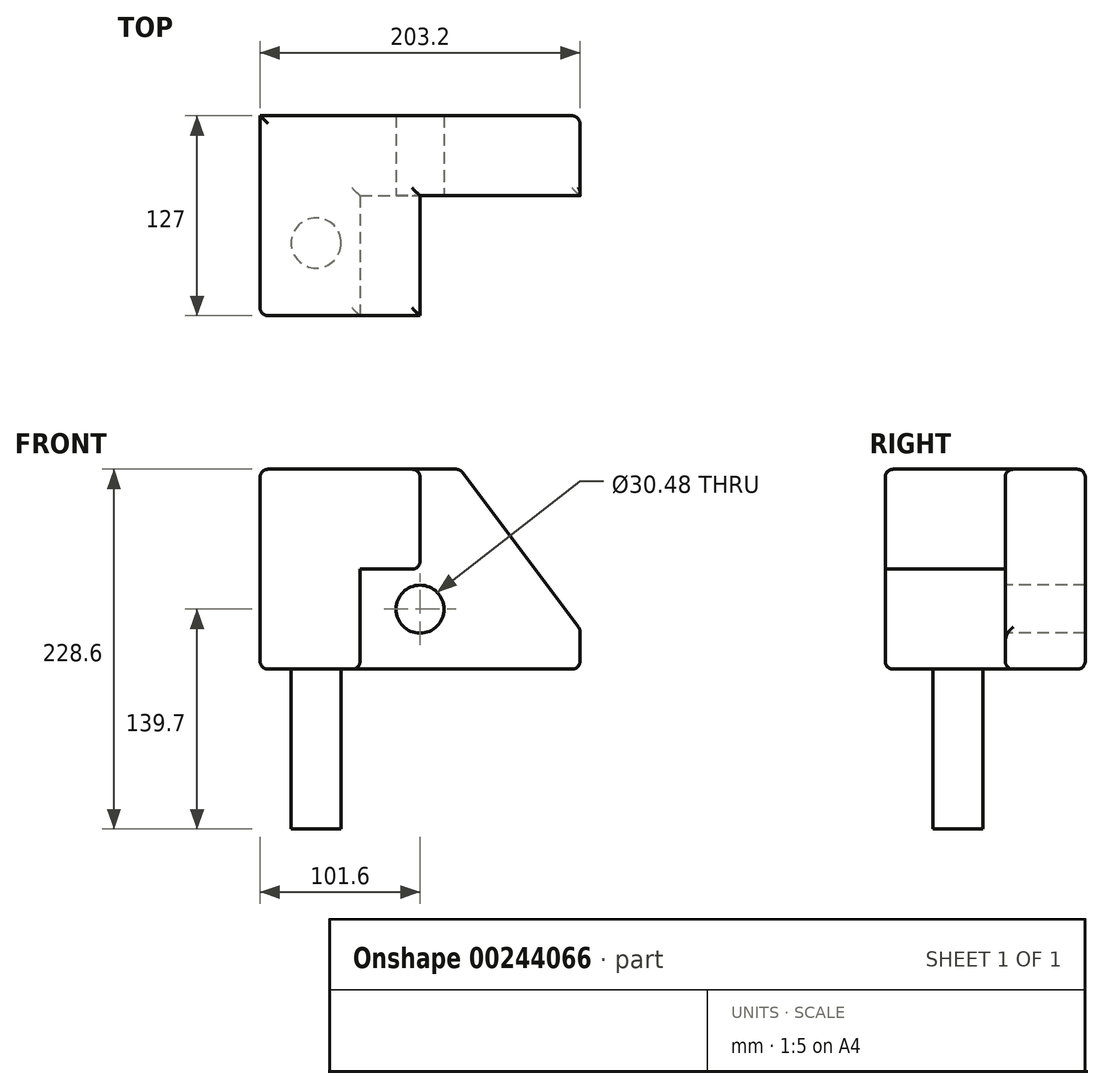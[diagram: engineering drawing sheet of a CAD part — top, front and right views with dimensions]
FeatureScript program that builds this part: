
annotation { "Feature Type Name" : "Feature", "Feature Type Description" : "" }
export const myFeature = defineFeature(function(context is Context, id is Id, definition is map)
    precondition{}
    {
        {
            var Q0;
            Q0=qCreatedBy(makeId("Front.planeOp"),FACE);
            var sketch = newSketch(context, id + "F0", { "sketchPlane" : qUnion([Q0])});
            skLineSegment(sketch, "E0.bottom", {"start": v(-101.6, 63.5) * mm, "end": v(101.6, 63.5) * mm});
            skLineSegment(sketch, "E0.top", {"start": v(-101.6, -63.5) * mm, "end": v(101.6, -63.5) * mm});
            skLineSegment(sketch, "E0.left", {"start": v(-101.6, 63.5) * mm, "end": v(-101.6, -63.5) * mm});
            skLineSegment(sketch, "E0.right", {"start": v(101.6, 63.5) * mm, "end": v(101.6, -63.5) * mm});
            skPoint(sketch, "E0.middle", {"position": v(0, 0) * mm});
            skSolve(sketch);
        }
        {
            var Q0;
            Q0=makeQuery(id+"F0.imprint","IMPRINT",FACE,{"disambiguationData":[TD([[makeQuery(id+"F0.imprint","IMPRINT",EDGE,{"derivedFrom":sQuery(id+"F0.wireOp",EDGE,"E0.bottom")}),-1.0]])]});
            extrude(context, id + "F1", {"entities" : qUnion([Q0]), "depth" : 127 * mm});
        }
        {
            var Q0;
            Q0=makeQuery(id+"F1.opExtrude","CAP_FACE",FACE,{"disambiguationData":[OSD([sQuery(id+"F0.wireOp",EDGE,"E0.bottom"),sQuery(id+"F0.wireOp",EDGE,"E0.top"),sQuery(id+"F0.wireOp",EDGE,"E0.left"),sQuery(id+"F0.wireOp",EDGE,"E0.right")])],"isStart":false});
            var sketch = newSketch(context, id + "F2", { "sketchPlane" : qUnion([Q0])});
            skLineSegment(sketch, "E1", {"start": v(-101.6, -63.5) * mm, "end": v(-38.1, -63.5) * mm});
            skLineSegment(sketch, "E2", {"start": v(-38.1, -63.5) * mm, "end": v(-38.1, 0) * mm});
            skLineSegment(sketch, "E3", {"start": v(-38.1, 0) * mm, "end": v(0, 0) * mm});
            skLineSegment(sketch, "E4", {"start": v(0, 0) * mm, "end": v(0, 63.5) * mm});
            skLineSegment(sketch, "E5", {"start": v(0, 63.5) * mm, "end": v(-101.6, 63.5) * mm});
            skLineSegment(sketch, "E6", {"start": v(-101.6, 63.5) * mm, "end": v(-101.6, -63.5) * mm});
            skSolve(sketch);
        }
        {
            var Q0;
            {var subQ3=sQuery(id+"F2.wireOp",EDGE,"E2");Q0=makeQuery(id+"F2.imprint","IMPRINT",FACE,{"disambiguationData":[TD([[makeQuery(id+"F2.imprint","IMPRINT",EDGE,{"derivedFrom":subQ3}),-1.0]])]});}
            extrude(context, id + "F3", {"entities" : qUnion([Q0]), "operationType" : NewBodyOperationType.REMOVE, "oppositeDirection" : true, "depth" : 76.2 * mm});
        }
        {
            var Q0;
            Q0=makeQuery(id+"F1.opExtrude","SWEPT_EDGE",EDGE,{"disambiguationData":[OSD([sQuery(id+"F0.wireOp",EDGE,"E0.bottom"),sQuery(id+"F0.wireOp",EDGE,"E0.right")])]});
            chamfer(context, id + "F4", {"entities" : qUnion([Q0]), "chamferType" : ChamferType.TWO_OFFSETS, "width1" : 76.2 * mm, "oppositeDirection" : false, "width2" : 101.6 * mm, "tangentPropagation" : true});
        }
        {
            var Q0;
            Q0=makeQuery(id+"F1.opExtrude","CAP_EDGE",EDGE,{"disambiguationData":[OSD([sQuery(id+"F0.wireOp",EDGE,"E0.bottom")])],"isStart":false});
            var Q1;
            Q1=makeQuery(id+"F1.opExtrude","SWEPT_EDGE",EDGE,{"disambiguationData":[OSD([sQuery(id+"F0.wireOp",EDGE,"E0.bottom"),sQuery(id+"F0.wireOp",EDGE,"E0.left")])]});
            var Q2;
            Q2=makeQuery(id+"F3.boolean.opBoolean","COPY",EDGE,{"derivedFrom":makeQuery(id+"F3.opExtrude","CAP_EDGE",EDGE,{"disambiguationData":[OSD([sQuery(id+"F0.wireOp",EDGE,"E0.bottom")])],"isStart":false})});
            var Q3;
            Q3=makeQuery(id+"F3.boolean.opBoolean","COPY",EDGE,{"derivedFrom":makeQuery(id+"F3.opExtrude","CAP_EDGE",EDGE,{"disambiguationData":[OSD([sQuery(id+"F2.wireOp",EDGE,"E4")])],"isStart":true})});
            var Q4;
            Q4=makeQuery(id+"F3.boolean.opBoolean","COPY",EDGE,{"derivedFrom":makeQuery(id+"F3.opExtrude","CAP_EDGE",EDGE,{"disambiguationData":[OSD([sQuery(id+"F2.wireOp",EDGE,"E3")])],"isStart":true})});
            var Q5;
            Q5=makeQuery(id+"F3.boolean.opBoolean","COPY",EDGE,{"derivedFrom":makeQuery(id+"F3.opExtrude","CAP_EDGE",EDGE,{"disambiguationData":[OSD([sQuery(id+"F2.wireOp",EDGE,"E2")])],"isStart":true})});
            var Q6;
            Q6=makeQuery(id+"F1.opExtrude","CAP_EDGE",EDGE,{"disambiguationData":[OSD([sQuery(id+"F0.wireOp",EDGE,"E0.top")])],"isStart":false});
            var Q7;
            Q7=makeQuery(id+"F1.opExtrude","CAP_EDGE",EDGE,{"disambiguationData":[OSD([sQuery(id+"F0.wireOp",EDGE,"E0.left")])],"isStart":false});
            var Q8;
            Q8=makeQuery(id+"F3.boolean.opBoolean","COPY",EDGE,{"derivedFrom":makeQuery(id+"F3.opExtrude","SWEPT_EDGE",EDGE,{"disambiguationData":[OSD([sQuery(id+"F0.wireOp",EDGE,"E0.top"),sQuery(id+"F2.wireOp",EDGE,"E1"),sQuery(id+"F2.wireOp",EDGE,"E2")])]})});
            var Q9;
            Q9=makeQuery(id+"F3.boolean.opBoolean","COPY",EDGE,{"derivedFrom":makeQuery(id+"F3.opExtrude","CAP_EDGE",EDGE,{"disambiguationData":[OSD([sQuery(id+"F0.wireOp",EDGE,"E0.top")])],"isStart":false})});
            var Q10;
            Q10=makeQuery(id+"F1.opExtrude","SWEPT_FACE",FACE,{"disambiguationData":[OSD([sQuery(id+"F0.wireOp",EDGE,"E0.top")])]});
            var Q11;
            Q11=makeQuery(id+"F1.opExtrude","SWEPT_FACE",FACE,{"disambiguationData":[OSD([sQuery(id+"F0.wireOp",EDGE,"E0.bottom")])]});
            var Q12;
            Q12=makeQuery(id+"F3.boolean.opBoolean","COPY",EDGE,{"derivedFrom":makeQuery(id+"F3.opExtrude","SWEPT_EDGE",EDGE,{"disambiguationData":[OSD([sQuery(id+"F2.wireOp",EDGE,"E3"),sQuery(id+"F2.wireOp",EDGE,"E4")])]})});
            var Q13;
            {var subQ0=sQuery(id+"F0.wireOp",EDGE,"E0.right");Q13=makeQuery(id+"F4.opChamfer","BLEND_EDGE",EDGE,{"blendedFrom":[makeQuery(id+"F1.opExtrude","SWEPT_EDGE",EDGE,{"disambiguationData":[OSD([sQuery(id+"F0.wireOp",EDGE,"E0.bottom"),subQ0])]}),makeQuery(id+"F1.opExtrude","SWEPT_FACE",FACE,{"disambiguationData":[OSD([subQ0])]})],"blendedInto":[makeQuery(id+"F1.opExtrude","SWEPT_FACE",FACE,{"disambiguationData":[OSD([subQ0])]})]});}
            var Q14;
            {var subQ0=sQuery(id+"F0.wireOp",EDGE,"E0.right");var subQ1=sQuery(id+"F0.wireOp",EDGE,"E0.bottom");Q14=makeQuery(id+"F4.opChamfer","BLEND_EDGE",EDGE,{"blendedFrom":[makeQuery(id+"F1.opExtrude","SWEPT_EDGE",EDGE,{"disambiguationData":[OSD([subQ1,subQ0])]}),makeQuery(id+"F3.boolean.opBoolean","COPY",FACE,{"derivedFrom":makeQuery(id+"F3.opExtrude","CAP_FACE",FACE,{"disambiguationData":[OSD([subQ1,sQuery(id+"F0.wireOp",EDGE,"E0.top"),subQ0,sQuery(id+"F2.wireOp",EDGE,"E2"),sQuery(id+"F2.wireOp",EDGE,"E3"),sQuery(id+"F2.wireOp",EDGE,"E4")])],"isStart":false})})],"blendedInto":[makeQuery(id+"F3.boolean.opBoolean","COPY",FACE,{"derivedFrom":makeQuery(id+"F3.opExtrude","CAP_FACE",FACE,{"disambiguationData":[OSD([subQ1,sQuery(id+"F0.wireOp",EDGE,"E0.top"),subQ0,sQuery(id+"F2.wireOp",EDGE,"E2"),sQuery(id+"F2.wireOp",EDGE,"E3"),sQuery(id+"F2.wireOp",EDGE,"E4")])],"isStart":false})})]});}
            var Q15;
            {var subQ0=sQuery(id+"F0.wireOp",EDGE,"E0.right");var subQ1=sQuery(id+"F0.wireOp",EDGE,"E0.bottom");Q15=makeQuery(id+"F4.opChamfer","BLEND_EDGE",EDGE,{"blendedFrom":[makeQuery(id+"F1.opExtrude","SWEPT_EDGE",EDGE,{"disambiguationData":[OSD([subQ1,subQ0])]}),makeQuery(id+"F1.opExtrude","CAP_FACE",FACE,{"disambiguationData":[OSD([subQ1,sQuery(id+"F0.wireOp",EDGE,"E0.top"),sQuery(id+"F0.wireOp",EDGE,"E0.left"),subQ0])],"isStart":true})],"blendedInto":[makeQuery(id+"F1.opExtrude","CAP_FACE",FACE,{"disambiguationData":[OSD([subQ1,sQuery(id+"F0.wireOp",EDGE,"E0.top"),sQuery(id+"F0.wireOp",EDGE,"E0.left"),subQ0])],"isStart":true})]});}
            var Q16;
            Q16=makeQuery(id+"F3.boolean.opBoolean","COPY",EDGE,{"derivedFrom":makeQuery(id+"F3.opExtrude","CAP_EDGE",EDGE,{"disambiguationData":[OSD([sQuery(id+"F0.wireOp",EDGE,"E0.right")])],"isStart":false})});
            var Q17;
            Q17=makeQuery(id+"F1.opExtrude","CAP_EDGE",EDGE,{"disambiguationData":[OSD([sQuery(id+"F0.wireOp",EDGE,"E0.right")])],"isStart":true});
            fillet(context, id + "F5", {"entities" : qUnion([Q0, Q1, Q2, Q3, Q4, Q5, Q6, Q7, Q8, Q9, Q10, Q11, Q12, Q13, Q14, Q15, Q16, Q17]), "radius" : 5.08 * mm, "tangentPropagation" : true, "allowEdgeOverflow" : false});
        }
        {
            var Q0;
            Q0=makeQuery(id+"F3.boolean.opBoolean","COPY",FACE,{"derivedFrom":makeQuery(id+"F3.opExtrude","CAP_FACE",FACE,{"disambiguationData":[OSD([sQuery(id+"F0.wireOp",EDGE,"E0.bottom"),sQuery(id+"F0.wireOp",EDGE,"E0.top"),sQuery(id+"F0.wireOp",EDGE,"E0.right"),sQuery(id+"F2.wireOp",EDGE,"E2"),sQuery(id+"F2.wireOp",EDGE,"E3"),sQuery(id+"F2.wireOp",EDGE,"E4")])],"isStart":false})});
            var sketch = newSketch(context, id + "F6", { "sketchPlane" : qUnion([Q0])});
            skCircle(sketch, "E7", {"center": v(0, -25.4) * mm, "radius": 15.24 * mm});
            skSolve(sketch);
        }
        {
            var Q0;
            Q0=makeQuery(id+"F6.imprint","IMPRINT",FACE,{"disambiguationData":[TD([[makeQuery(id+"F6.imprint","IMPRINT",EDGE,{"derivedFrom":sQuery(id+"F6.wireOp",EDGE,"E7")}),1.0]])]});
            extrude(context, id + "F7", {"entities" : qUnion([Q0]), "operationType" : NewBodyOperationType.REMOVE, "oppositeDirection" : true, "depth" : 381 * mm});
        }
        {
            var Q0;
            Q0=makeQuery(id+"F1.opExtrude","SWEPT_FACE",FACE,{"disambiguationData":[OSD([sQuery(id+"F0.wireOp",EDGE,"E0.top")])]});
            var sketch = newSketch(context, id + "F8", { "sketchPlane" : qUnion([Q0])});
            skCircle(sketch, "E8", {"center": v(-66, 80.77) * mm, "radius": 15.89 * mm});
            skSolve(sketch);
        }
        {
            var Q0;
            Q0=makeQuery(id+"F8.imprint","IMPRINT",FACE,{"disambiguationData":[TD([[makeQuery(id+"F8.imprint","IMPRINT",EDGE,{"derivedFrom":sQuery(id+"F8.wireOp",EDGE,"E8")}),1.0]])]});
            extrude(context, id + "F9", {"entities" : qUnion([Q0]), "depth" : 101.6 * mm});
        }
    });
